# Revit family: Windows_Dbl_All_Bars
name_source: partatom
category: Windows
revit_build: Autodesk Revit 2015 (Build: 20140117_1515(x64)
units: mm (PartAtom-declared; Revit-internal decimal feet)

## types (6) — shared parameters
Analytic Construction = 1/8 in Pilkington single glazing
Cavity Closer Depth = 85 mm  [stored 0.278871 ft]
Cavity Closer Offset from Ext = 102.5 mm  [stored 0.336286 ft]
Cavity Closer Width = 50 mm  [stored 0.164042 ft]
Cill Depth = 87.5 mm  [stored 0.287073 ft]
Construction Type Id = GSP4R
Default Head Height = 2110 mm  [stored 6.92257 ft]
Frame Depth = 65 mm  [stored 0.213255 ft]
FrameOffset - External = 50 mm  [stored 0.164042 ft]
Glazing Bar Thickness = 20 mm  [stored 0.0656168 ft]
Glazing Thickness = 24 mm  [stored 0.0787402 ft]
Heat Transfer Coefficient (U) = 3.6886 W/(m²·K)
Keynote = L10
Manufacturer = Revit
Material Frame = Window Frame
Material Glass = Glass
Material Glazing Bars = Window Frame
Material Trim = Window Frame
Operation = DoublePanelVertical
Solar Heat Gain Coefficient = 0.78
Vis - Cavity Closers = Yes
Vis - Glazing Bars = Yes
Visual Light Transmittance = 0.9
Wall Closure = By host
Window Board Extension = 25 mm  [stored 0.082021 ft]
Window Board Projection = 25 mm  [stored 0.082021 ft]
Wrap Layers (Ext) from Ext = 102.5 mm  [stored 0.336286 ft]
Wrap Layers (Int) from Ext = 177.5 mm  [stored 0.582349 ft]

## per-type parameters (varying)
| type | Height | Rough Height | Rough Width | Width |
| 910x910mm | 910 mm  [stored 2.98556 ft] | 910 mm  [stored 2.98556 ft] | 910 mm  [stored 2.98556 ft] | 910 mm  [stored 2.98556 ft] |
| 910x1210mm | 1210 mm  [stored 3.96982 ft] | 1210 mm  [stored 3.96982 ft] | 910 mm  [stored 2.98556 ft] | 910 mm  [stored 2.98556 ft] |
| 1360x910mm | 910 mm  [stored 2.98556 ft] | 910 mm  [stored 2.98556 ft] | 1360 mm  [stored 4.46194 ft] | 1360 mm  [stored 4.46194 ft] |
| 1360x1210mm | 1210 mm  [stored 3.96982 ft] | 1210 mm  [stored 3.96982 ft] | 1360 mm  [stored 4.46194 ft] | 1360 mm  [stored 4.46194 ft] |
| 1810x910mm | 910 mm  [stored 2.98556 ft] | 910 mm  [stored 2.98556 ft] | 1810 mm  [stored 5.93832 ft] | 1810 mm  [stored 5.93832 ft] |
| 1810x1210mm | 1210 mm  [stored 3.96982 ft] | 1210 mm  [stored 3.96982 ft] | 1810 mm  [stored 5.93832 ft] | 1810 mm  [stored 5.93832 ft] |

note: [stored X ft] marks values corroborated as IEEE doubles in the binary element streams (Revit-internal decimal feet)

## geometry (parser evidence)
native form markers: Sweep x2
no freeform markers — native parametric forms only
